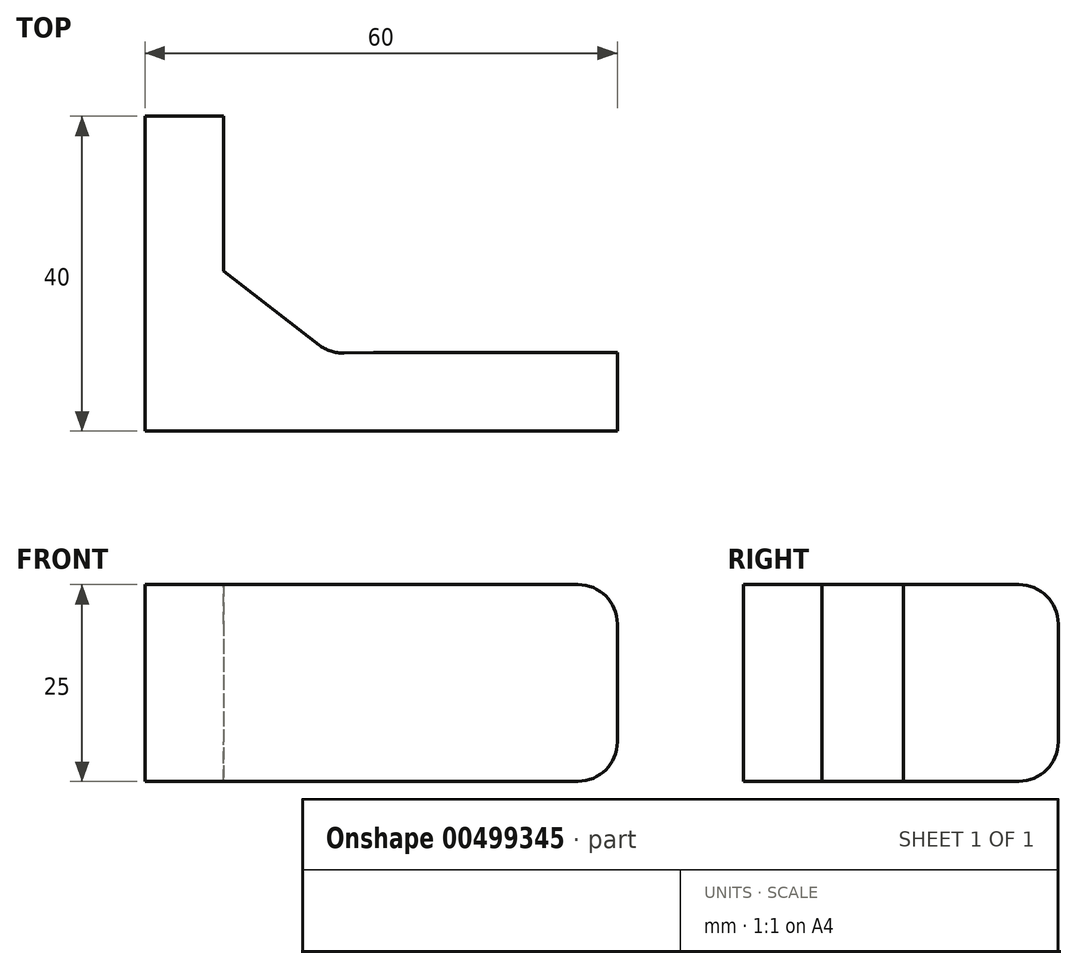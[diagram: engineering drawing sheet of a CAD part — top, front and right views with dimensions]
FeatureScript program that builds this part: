
annotation { "Feature Type Name" : "Feature", "Feature Type Description" : "" }
export const myFeature = defineFeature(function(context is Context, id is Id, definition is map)
    precondition{}
    {
        {
            var Q0;
            Q0=qCreatedBy(makeId("Top.planeOp"),FACE);
            var sketch = newSketch(context, id + "F0", { "sketchPlane" : qUnion([Q0])});
            skLineSegment(sketch, "E0", {"start": v(0, 0) * mm, "end": v(0, 40) * mm});
            skLineSegment(sketch, "E1", {"start": v(0, 40) * mm, "end": v(10, 40) * mm});
            skLineSegment(sketch, "E2", {"start": v(0, 0) * mm, "end": v(60, 0) * mm});
            skLineSegment(sketch, "E3", {"start": v(60, 0) * mm, "end": v(60, 10) * mm});
            skLineSegment(sketch, "E4", {"start": v(60, 10) * mm, "end": v(29.1, 10) * mm});
            skLineSegment(sketch, "E5", {"start": v(10, 40) * mm, "end": v(10, 20.35) * mm});
            skLineSegment(sketch, "E6", {"start": v(10, 20.35) * mm, "end": v(23.52, 9.86) * mm});
            skLineSegment(sketch, "E7", {"start": v(23.52, 9.86) * mm, "end": v(29.1, 10) * mm});
            skSolve(sketch);
        }
        {
            var Q0;
            Q0=makeQuery(id+"F0.imprint","IMPRINT",FACE,{"disambiguationData":[TD([[makeQuery(id+"F0.imprint","IMPRINT",EDGE,{"derivedFrom":sQuery(id+"F0.wireOp",EDGE,"E0")}),-1.0]])]});
            extrude(context, id + "F1", {"entities" : qUnion([Q0]), "depth" : 25 * mm});
        }
        {
            var Q0;
            Q0=makeQuery(id+"F1.opExtrude","CAP_EDGE",EDGE,{"disambiguationData":[OSD([sQuery(id+"F0.wireOp",EDGE,"E1")])],"isStart":true});
            var Q1;
            Q1=makeQuery(id+"F1.opExtrude","CAP_EDGE",EDGE,{"disambiguationData":[OSD([sQuery(id+"F0.wireOp",EDGE,"E1")])],"isStart":false});
            var Q2;
            Q2=makeQuery(id+"F1.opExtrude","CAP_EDGE",EDGE,{"disambiguationData":[OSD([sQuery(id+"F0.wireOp",EDGE,"E3")])],"isStart":false});
            var Q3;
            Q3=makeQuery(id+"F1.opExtrude","CAP_EDGE",EDGE,{"disambiguationData":[OSD([sQuery(id+"F0.wireOp",EDGE,"E3")])],"isStart":true});
            var Q4;
            Q4=makeQuery(id+"F1.opExtrude","SWEPT_EDGE",EDGE,{"disambiguationData":[OSD([sQuery(id+"F0.wireOp",EDGE,"E4"),sQuery(id+"F0.wireOp",EDGE,"E7")])]});
            var Q5;
            Q5=makeQuery(id+"F1.opExtrude","SWEPT_EDGE",EDGE,{"disambiguationData":[OSD([sQuery(id+"F0.wireOp",EDGE,"E6"),sQuery(id+"F0.wireOp",EDGE,"E7")])]});
            fillet(context, id + "F2", {"entities" : qUnion([Q0, Q1, Q2, Q3, Q4, Q5]), "radius" : 5 * mm, "tangentPropagation" : true, "allowEdgeOverflow" : false});
        }
    });
